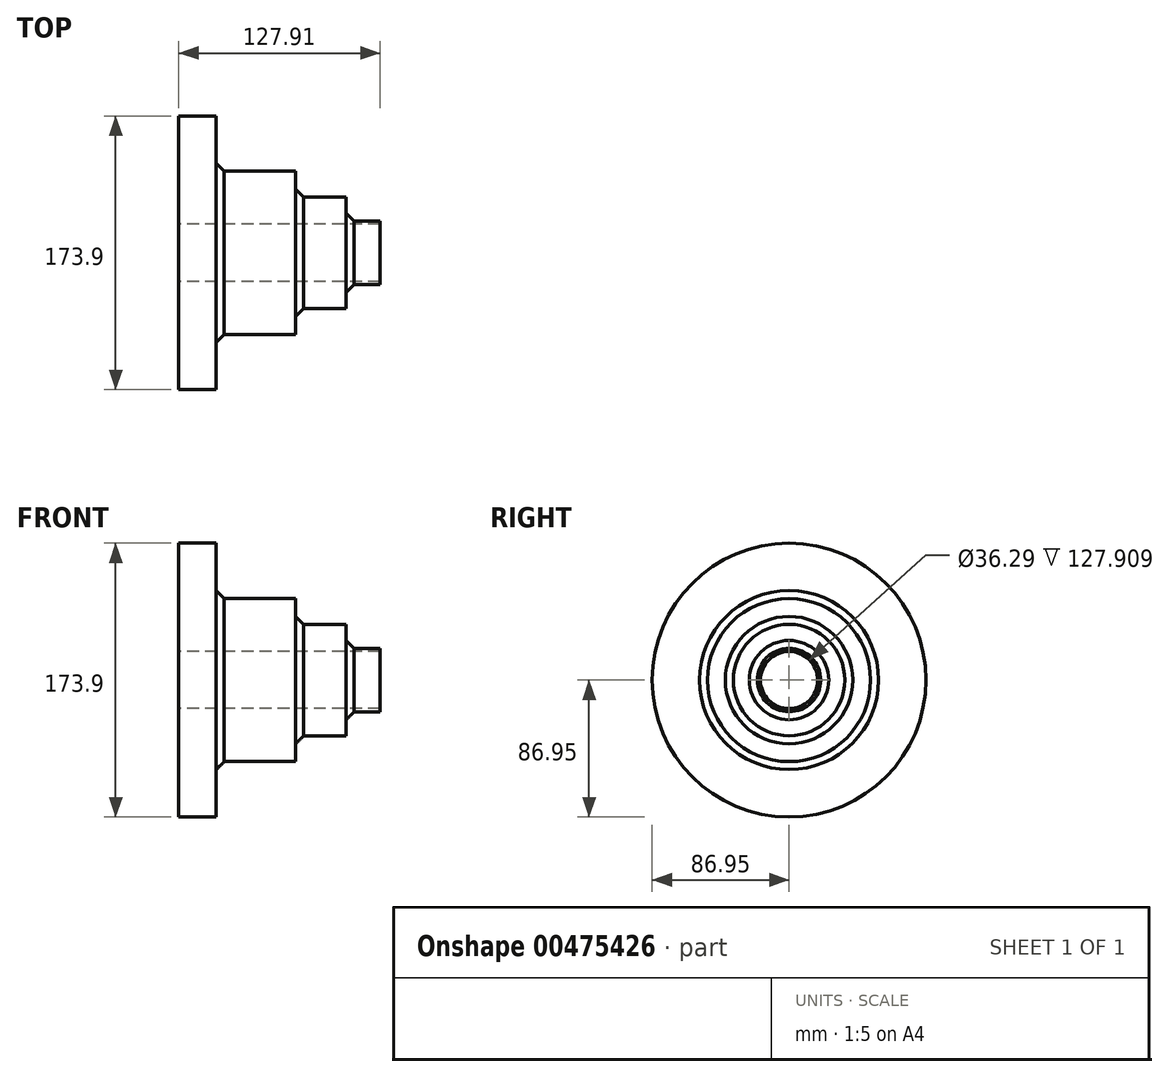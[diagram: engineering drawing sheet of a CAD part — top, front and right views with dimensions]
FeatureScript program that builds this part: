
annotation { "Feature Type Name" : "Feature", "Feature Type Description" : "" }
export const myFeature = defineFeature(function(context is Context, id is Id, definition is map)
    precondition{}
    {
        {
            var Q0;
            Q0=qCreatedBy(makeId("Front.planeOp"),FACE);
            var sketch = newSketch(context, id + "F0", { "sketchPlane" : qUnion([Q0])});
            skLineSegment(sketch, "E0", {"start": v(0, 86.95) * mm, "end": v(0, 51.78) * mm});
            skLineSegment(sketch, "E1", {"start": v(0, 51.78) * mm, "end": v(50.43, 51.78) * mm});
            skLineSegment(sketch, "E2", {"start": v(50.43, 51.78) * mm, "end": v(50.43, 35.38) * mm});
            skLineSegment(sketch, "E3", {"start": v(50.43, 35.38) * mm, "end": v(82.5, 35.38) * mm});
            skLineSegment(sketch, "E4", {"start": v(82.5, 35.38) * mm, "end": v(82.5, 20.12) * mm});
            skLineSegment(sketch, "E5", {"start": v(82.5, 20.12) * mm, "end": v(104.12, 20.12) * mm});
            skLineSegment(sketch, "E6", {"start": v(104.12, 20.12) * mm, "end": v(104.12, 0) * mm});
            skLineSegment(sketch, "E7", {"start": v(104.12, 0) * mm, "end": v(0, 0) * mm});
            skLineSegment(sketch, "E8", {"start": v(0, 0) * mm, "end": v(-23.8, 0) * mm});
            skLineSegment(sketch, "E9", {"start": v(-23.8, 0) * mm, "end": v(-23.8, 86.95) * mm});
            skLineSegment(sketch, "E10", {"start": v(-23.8, 86.95) * mm, "end": v(0, 86.95) * mm});
            skLineSegment(sketch, "E11", {"start": v(-85.91, 0) * mm, "end": v(-23.8, 0) * mm, "construction": true});
            skSolve(sketch);
        }
        {
            var Q0;
            Q0=makeQuery(id+"F0.imprint","IMPRINT",FACE,{"disambiguationData":[TD([[makeQuery(id+"F0.imprint","IMPRINT",EDGE,{"derivedFrom":sQuery(id+"F0.wireOp",EDGE,"E0")}),-1.0]])]});
            var Q1;
            Q1=sQuery(id+"F0.wireOp",EDGE,"E11");
            revolve(context, id + "F1", {"entities" : qUnion([Q0]), "axis" : qUnion([Q1]), "revolveType" : RevolveType.FULL});
        }
        {
            var Q0;
            Q0=makeQuery(id+"F1.opRevolve","SWEPT_EDGE",EDGE,{"disambiguationData":[OSD([sQuery(id+"F0.wireOp",EDGE,"E0"),sQuery(id+"F0.wireOp",EDGE,"E1")])]});
            chamfer(context, id + "F2", {"entities" : qUnion([Q0]), "width" : 5.08 * mm, "tangentPropagation" : true});
        }
        {
            var Q0;
            Q0=makeQuery(id+"F1.opRevolve","SWEPT_EDGE",EDGE,{"disambiguationData":[OSD([sQuery(id+"F0.wireOp",EDGE,"E2"),sQuery(id+"F0.wireOp",EDGE,"E3")])]});
            var Q1;
            Q1=makeQuery(id+"F1.opRevolve","SWEPT_EDGE",EDGE,{"disambiguationData":[OSD([sQuery(id+"F0.wireOp",EDGE,"E4"),sQuery(id+"F0.wireOp",EDGE,"E5")])]});
            chamfer(context, id + "F3", {"entities" : qUnion([Q0, Q1]), "width" : 5.08 * mm, "tangentPropagation" : true});
        }
        {
            var Q0;
            Q0=makeQuery(id+"F1.opRevolve","SWEPT_FACE",FACE,{"disambiguationData":[OSD([sQuery(id+"F0.wireOp",EDGE,"E9")])]});
            var sketch = newSketch(context, id + "F4", { "sketchPlane" : qUnion([Q0])});
            skCircle(sketch, "E12", {"center": v(0, 0) * mm, "radius": 18.15 * mm});
            skSolve(sketch);
        }
        {
            var Q0;
            Q0 = qSketchRegion(id + "F4", true);
            extrude(context, id + "F5", {"entities" : qUnion([Q0]), "operationType" : NewBodyOperationType.REMOVE, "endBound" : BoundingType.UP_TO_NEXT, "oppositeDirection" : true, "depth" : 25.4 * mm});
        }
    });
